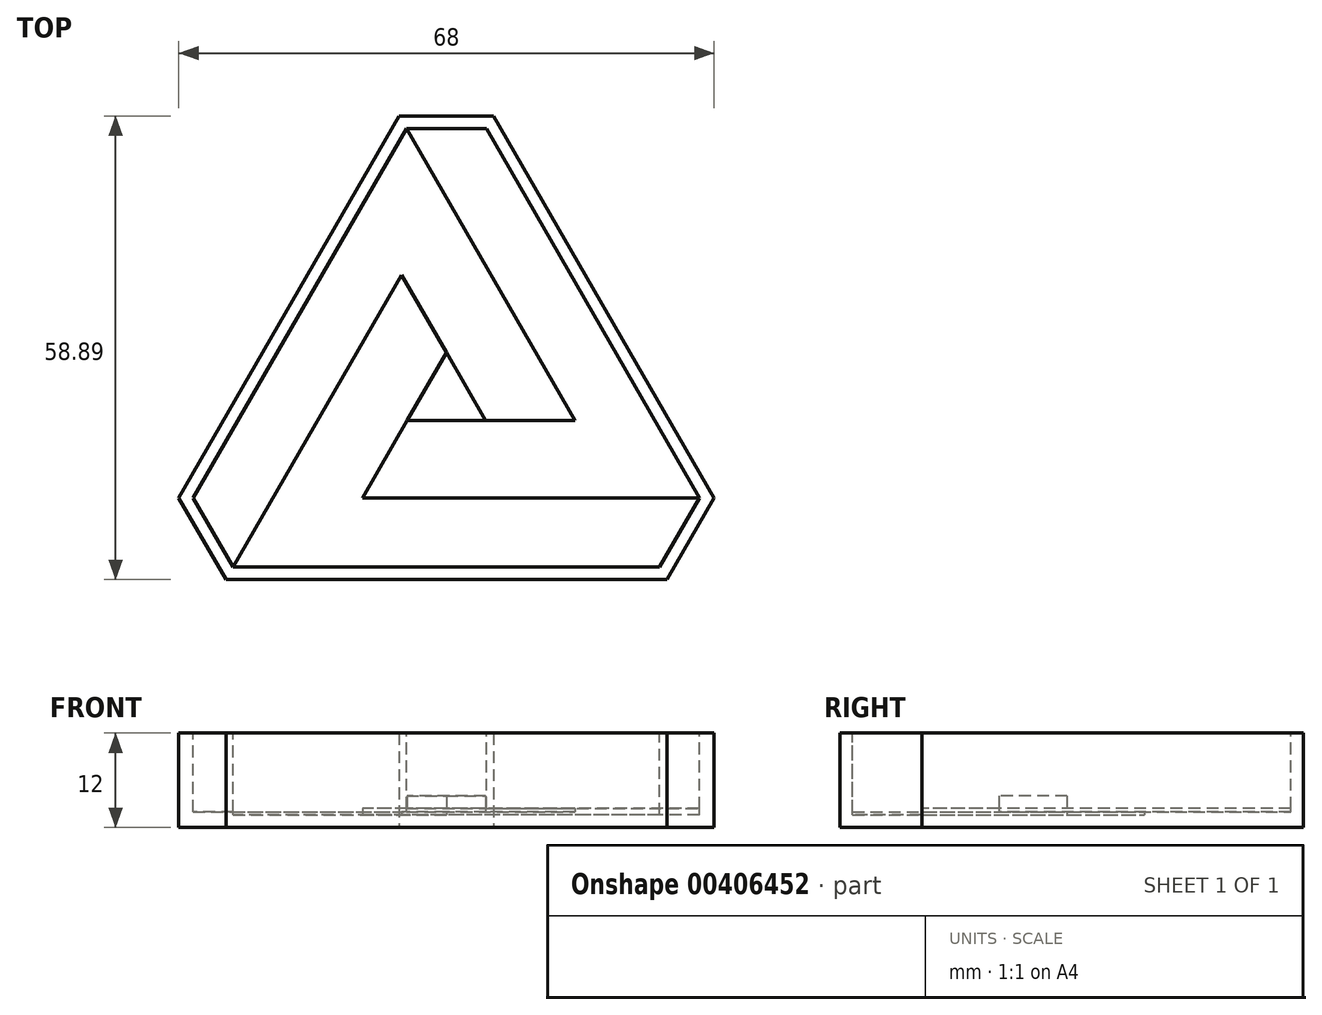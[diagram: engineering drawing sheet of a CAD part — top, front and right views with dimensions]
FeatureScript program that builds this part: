
annotation { "Feature Type Name" : "Feature", "Feature Type Description" : "" }
export const myFeature = defineFeature(function(context is Context, id is Id, definition is map)
    precondition{}
    {
        {
            assignVariable(context, id + "F0", {"name" : "walls", "anyValue" : 1.6 * mm});
        }
        {
            assignVariable(context, id + "F1", {"name" : "H", "anyValue" : 12 * mm});
        }
        {
            assignVariable(context, id + "F2", {"name" : "ramps", "anyValue" : .4 * mm});
        }
        {
            var Q0;
            Q0=qCreatedBy(makeId("Top.planeOp"),FACE);
            var sketch = newSketch(context, id + "F3", { "sketchPlane" : qUnion([Q0])});
            skCircle(sketch, "E0.cCircle", {"center": v(0, 0) * mm, "radius": 23.1 * mm, "construction": true});
            skLineSegment(sketch, "E0.0", {"start": v(40, -23.1) * mm, "end": v(-40, -23.1) * mm});
            skLineSegment(sketch, "E0.1", {"start": v(-40, -23.1) * mm, "end": v(0, 46.19) * mm});
            skLineSegment(sketch, "E0.2", {"start": v(0, 46.19) * mm, "end": v(40, -23.1) * mm});
            skPoint(sketch, "E0.0.midPoint", {"position": v(0, -23.1) * mm});
            skCircle(sketch, "E1.1.1", {"center": v(0.24, 0.42) * mm, "radius": 39.98 * mm, "construction": true});
            skLineSegment(sketch, "E2", {"start": v(-6, 35.8) * mm, "end": v(6, 35.8) * mm});
            skLineSegment(sketch, "E3.1.0", {"start": v(-28, -23.1) * mm, "end": v(-34, -12.7) * mm});
            skLineSegment(sketch, "E3.2.0", {"start": v(34, -12.7) * mm, "end": v(28, -23.1) * mm});
            skSolve(sketch);
        }
        {
            var Q0;
            {var subQ0=sQuery(id+"F3.wireOp",EDGE,"E2");Q0=makeQuery(id+"F3.imprint","IMPRINT",FACE,{"disambiguationData":[TD([[makeQuery(id+"F3.imprint","IMPRINT",EDGE,{"derivedFrom":subQ0}),-1.0]])]});}
            extrude(context, id + "F4", {"entities" : qUnion([Q0]), "depth" : getVariable(context, 'H')});
        }
        {
            var Q0;
            Q0=makeQuery(id+"F4.opExtrude","CAP_FACE",FACE,{"disambiguationData":[OSD([sQuery(id+"F3.wireOp",EDGE,"E0.0"),sQuery(id+"F3.wireOp",EDGE,"E0.1"),sQuery(id+"F3.wireOp",EDGE,"E0.2"),sQuery(id+"F3.wireOp",EDGE,"E2"),sQuery(id+"F3.wireOp",EDGE,"E3.1.0"),sQuery(id+"F3.wireOp",EDGE,"E3.2.0")])],"isStart":false});
            var sketch = newSketch(context, id + "F5", { "sketchPlane" : qUnion([Q0])});
            skLineSegment(sketch, "E4.0", {"start": v(5.08, 34.2) * mm, "end": v(32.15, -12.7) * mm});
            skLineSegment(sketch, "E4.1", {"start": v(27.08, -21.5) * mm, "end": v(-27.08, -21.5) * mm});
            skLineSegment(sketch, "E4.2", {"start": v(-27.08, -21.5) * mm, "end": v(-32.15, -12.7) * mm});
            skLineSegment(sketch, "E4.3", {"start": v(32.15, -12.7) * mm, "end": v(27.08, -21.5) * mm});
            skLineSegment(sketch, "E4.4", {"start": v(-32.15, -12.7) * mm, "end": v(-5.08, 34.2) * mm});
            skLineSegment(sketch, "E4.5", {"start": v(-5.08, 34.2) * mm, "end": v(5.08, 34.2) * mm});
            skSolve(sketch);
        }
        {
            var Q0;
            Q0=makeQuery(id+"F5.imprint","IMPRINT",FACE,{"disambiguationData":[TD([[makeQuery(id+"F5.imprint","IMPRINT",EDGE,{"derivedFrom":sQuery(id+"F5.wireOp",EDGE,"E4.0")}),-1.0]])]});
            extrude(context, id + "F6", {"entities" : qUnion([Q0]), "operationType" : NewBodyOperationType.REMOVE, "oppositeDirection" : true, "depth" : getVariable(context, 'H') - getVariable(context, 'walls')});
        }
        {
            var Q0;
            Q0=makeQuery(id+"F6.boolean.opBoolean","COPY",FACE,{"derivedFrom":makeQuery(id+"F6.opExtrude","CAP_FACE",FACE,{"disambiguationData":[OSD([sQuery(id+"F5.wireOp",EDGE,"E4.0"),sQuery(id+"F5.wireOp",EDGE,"E4.1"),sQuery(id+"F5.wireOp",EDGE,"E4.2"),sQuery(id+"F5.wireOp",EDGE,"E4.3"),sQuery(id+"F5.wireOp",EDGE,"E4.4"),sQuery(id+"F5.wireOp",EDGE,"E4.5")])],"isStart":false})});
            var sketch = newSketch(context, id + "F7", { "sketchPlane" : qUnion([Q0])});
            skCircle(sketch, "E5.cCircle", {"center": v(0, 0) * mm, "radius": 2.89 * mm, "construction": true});
            skLineSegment(sketch, "E5.0", {"start": v(5, -2.89) * mm, "end": v(-5, -2.89) * mm});
            skLineSegment(sketch, "E5.1", {"start": v(-5, -2.89) * mm, "end": v(0, 5.77) * mm});
            skLineSegment(sketch, "E5.2", {"start": v(0, 5.77) * mm, "end": v(5, -2.89) * mm});
            skPoint(sketch, "E5.0.midPoint", {"position": v(0, -2.89) * mm});
            skSolve(sketch);
        }
        {
            var Q0;
            Q0=makeQuery(id+"F7.imprint","IMPRINT",FACE,{"disambiguationData":[TD([[makeQuery(id+"F7.imprint","IMPRINT",EDGE,{"derivedFrom":sQuery(id+"F7.wireOp",EDGE,"E5.0")}),-1.0]])]});
            extrude(context, id + "F8", {"entities" : qUnion([Q0]), "operationType" : NewBodyOperationType.ADD, "depth" : 6 * getVariable(context, 'ramps')});
        }
        {
            var Q0;
            Q0=makeQuery(id+"F6.boolean.opBoolean","COPY",FACE,{"derivedFrom":makeQuery(id+"F6.opExtrude","CAP_FACE",FACE,{"disambiguationData":[OSD([sQuery(id+"F5.wireOp",EDGE,"E4.0"),sQuery(id+"F5.wireOp",EDGE,"E4.1"),sQuery(id+"F5.wireOp",EDGE,"E4.2"),sQuery(id+"F5.wireOp",EDGE,"E4.3"),sQuery(id+"F5.wireOp",EDGE,"E4.4"),sQuery(id+"F5.wireOp",EDGE,"E4.5")])],"isStart":false})});
            var sketch = newSketch(context, id + "F9", { "sketchPlane" : qUnion([Q0])});
            skLineSegment(sketch, "E6", {"start": v(-5.08, 34.2) * mm, "end": v(16.33, -2.89) * mm});
            skLineSegment(sketch, "E7", {"start": v(16.33, -2.89) * mm, "end": v(5, -2.89) * mm});
            skLineSegment(sketch, "E8", {"start": v(-27.08, -21.5) * mm, "end": v(0, 25.4) * mm});
            skLineSegment(sketch, "E9", {"start": v(0, 5.77) * mm, "end": v(-5.67, 15.59) * mm});
            skSolve(sketch);
        }
        {
            var Q0;
            {var subQ4=makeQuery(id+"F6.boolean.opBoolean","COPY",EDGE,{"derivedFrom":makeQuery(id+"F6.opExtrude","CAP_EDGE",EDGE,{"disambiguationData":[OSD([sQuery(id+"F5.wireOp",EDGE,"E4.2")])],"isStart":false})});Q0=makeQuery(id+"F9.imprint","IMPRINT",FACE,{"disambiguationData":[TD([[makeQuery(id+"F9.imprint","IMPRINT",EDGE,{"derivedFrom":subQ4}),-1.0]])]});}
            var Q1;
            {var subQ4=sQuery(id+"F9.wireOp",EDGE,"E7");Q1=makeQuery(id+"F9.imprint","IMPRINT",FACE,{"disambiguationData":[TD([[makeQuery(id+"F9.imprint","IMPRINT",EDGE,{"derivedFrom":subQ4}),-1.0]])]});}
            extrude(context, id + "F10", {"entities" : qUnion([Q0, Q1]), "operationType" : NewBodyOperationType.ADD, "depth" : getVariable(context, 'ramps')});
        }
        {
            var Q0;
            Q0=makeQuery(id+"F6.boolean.opBoolean","COPY",FACE,{"derivedFrom":makeQuery(id+"F6.opExtrude","CAP_FACE",FACE,{"disambiguationData":[OSD([sQuery(id+"F5.wireOp",EDGE,"E4.0"),sQuery(id+"F5.wireOp",EDGE,"E4.1"),sQuery(id+"F5.wireOp",EDGE,"E4.2"),sQuery(id+"F5.wireOp",EDGE,"E4.3"),sQuery(id+"F5.wireOp",EDGE,"E4.4"),sQuery(id+"F5.wireOp",EDGE,"E4.5")])],"isStart":false})});
            var sketch = newSketch(context, id + "F11", { "sketchPlane" : qUnion([Q0])});
            skLineSegment(sketch, "E10", {"start": v(32.15, -12.7) * mm, "end": v(-22, -12.7) * mm});
            skLineSegment(sketch, "E11", {"start": v(-5, -2.89) * mm, "end": v(-10.67, -12.7) * mm});
            skSolve(sketch);
        }
        {
            var Q0;
            {var subQ1=sQuery(id+"F11.wireOp",EDGE,"E11");Q0=makeQuery(id+"F11.imprint","IMPRINT",FACE,{"disambiguationData":[TD([[makeQuery(id+"F11.imprint","IMPRINT",EDGE,{"derivedFrom":subQ1}),1.0]])]});}
            extrude(context, id + "F12", {"entities" : qUnion([Q0]), "operationType" : NewBodyOperationType.ADD, "depth" : 2 * getVariable(context, 'ramps')});
        }
    });
